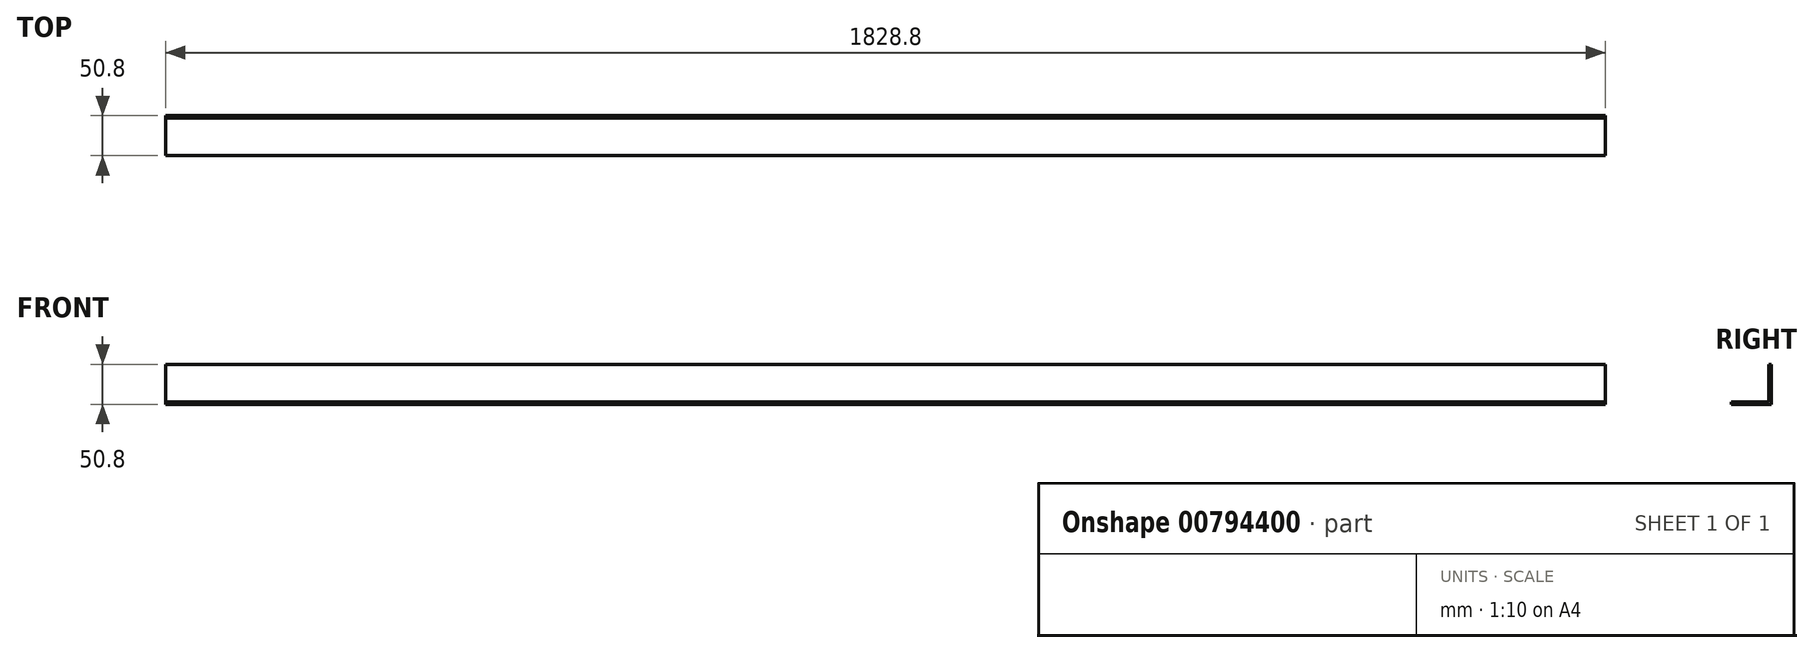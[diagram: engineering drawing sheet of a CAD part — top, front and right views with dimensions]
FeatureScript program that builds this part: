
annotation { "Feature Type Name" : "Feature", "Feature Type Description" : "" }
export const myFeature = defineFeature(function(context is Context, id is Id, definition is map)
    precondition{}
    {
        {
            var Q0;
            Q0=qCreatedBy(makeId("Right.planeOp"),FACE);
            var sketch = newSketch(context, id + "F0", { "sketchPlane" : qUnion([Q0])});
            skLineSegment(sketch, "E0.bottom", {"start": v(25.4, -25.4) * mm, "end": v(-25.4, -25.4) * mm, "construction": true});
            skLineSegment(sketch, "E0.top", {"start": v(25.4, 25.4) * mm, "end": v(-25.4, 25.4) * mm, "construction": true});
            skLineSegment(sketch, "E0.left", {"start": v(25.4, -25.4) * mm, "end": v(25.4, 25.4) * mm, "construction": true});
            skLineSegment(sketch, "E0.right", {"start": v(-25.4, -25.4) * mm, "end": v(-25.4, 25.4) * mm, "construction": true});
            skPoint(sketch, "E0.middle", {"position": v(0, 0) * mm});
            skLineSegment(sketch, "E1.0", {"start": v(22.23, -22.23) * mm, "end": v(22.23, 25.4) * mm});
            skLineSegment(sketch, "E2.0", {"start": v(22.23, -22.23) * mm, "end": v(-25.4, -22.23) * mm});
            skLineSegment(sketch, "E3", {"start": v(-25.4, -22.23) * mm, "end": v(-25.4, -25.4) * mm});
            skLineSegment(sketch, "E4", {"start": v(25.4, -25.4) * mm, "end": v(25.4, 25.4) * mm});
            skLineSegment(sketch, "E5", {"start": v(22.22, 25.4) * mm, "end": v(25.4, 25.4) * mm});
            skLineSegment(sketch, "E6", {"start": v(-25.4, -25.4) * mm, "end": v(25.4, -25.4) * mm});
            skSolve(sketch);
        }
        {
            var Q0;
            Q0=makeQuery(id+"F0.imprint","IMPRINT",FACE,{"disambiguationData":[TD([[makeQuery(id+"F0.imprint","IMPRINT",EDGE,{"derivedFrom":sQuery(id+"F0.wireOp",EDGE,"E1.0")}),-1.0]])]});
            extrude(context, id + "F1", {"entities" : qUnion([Q0]), "depth" : 914.4 * mm, "offsetDistance" : 25.4 * mm});
        }
        {
            var Q0;
            Q0=makeQuery(id+"F1.opExtrude","SWEPT_BODY",BODY,{"disambiguationData":[OSD([sQuery(id+"F0.wireOp",EDGE,"E1.0"),sQuery(id+"F0.wireOp",EDGE,"E2.0"),sQuery(id+"F0.wireOp",EDGE,"E3"),sQuery(id+"F0.wireOp",EDGE,"E4"),sQuery(id+"F0.wireOp",EDGE,"E5"),sQuery(id+"F0.wireOp",EDGE,"E6")])]});
            var Q1;
            Q1=qCreatedBy(makeId("Right.planeOp"),FACE);
            mirror(context, id + "F2", {"operationType" : NewBodyOperationType.ADD, "entities" : qUnion([Q0]), "mirrorPlane" : qUnion([Q1])});
        }
    });
